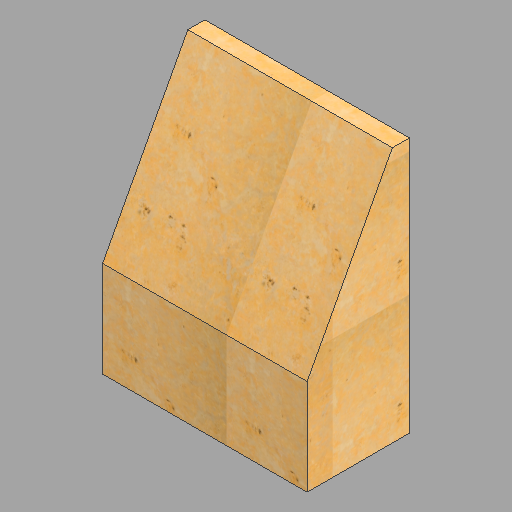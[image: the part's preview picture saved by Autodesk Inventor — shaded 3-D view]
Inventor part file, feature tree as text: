
AUTODESK INVENTOR PART (.ipt)
format: ipt  version: 2023 (Build 270158030, 158C)  size: 371,712 bytes
history: native  units: in
note: dims shown in document units (in); Inventor stores cm internally (conversion verified against a paired STEP export)
features: other x4, extrude x2, sketch x2
ambient origin geometry x8: Origin, YZ Plane, XZ Plane, XY Plane, X Axis, Y Axis, Z Axis, Center Point
bodies: Body1 (feature_tree)
feature tree (8):
  other  "Top"
  other  "Standard - Amber select"
  extrude  "Extrusion1"  Depth=0.3937in TaperAngle=0.0deg
  extrude  "Extrusion2"  Depth=12.5in
  other  "Top::Standard - Amber select"
  other  "TaggingFeature1"
  sketch  "Sketch1"  dims[d0=0.3937in d1=1.0in d2=0.0in]
  sketch  "Sketch2"  dims[d3=12.0in d4=8.0in d5=16.0in d6=16.0in d7=8.0in d8=1.5in d9=12.5in d10=0.0in]
